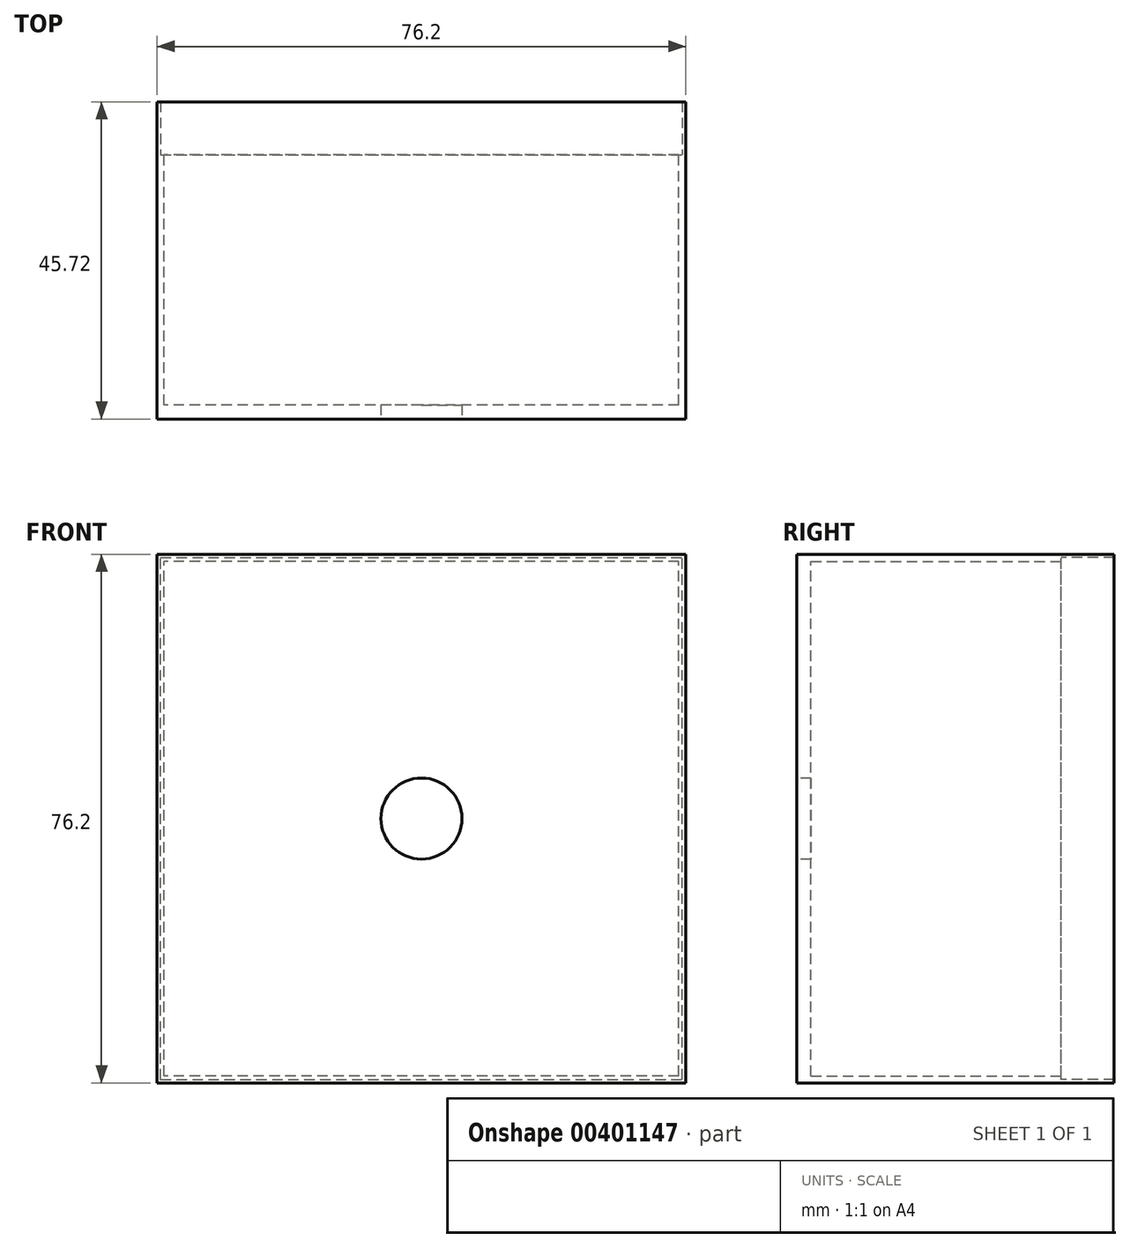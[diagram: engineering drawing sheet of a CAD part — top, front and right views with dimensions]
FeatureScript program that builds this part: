
annotation { "Feature Type Name" : "Feature", "Feature Type Description" : "" }
export const myFeature = defineFeature(function(context is Context, id is Id, definition is map)
    precondition{}
    {
        {
            var Q0;
            Q0=qCreatedBy(makeId("Front.planeOp"),FACE);
            var sketch = newSketch(context, id + "F0", { "sketchPlane" : qUnion([Q0])});
            skLineSegment(sketch, "E0.bottom", {"start": v(38.1, -38.1) * mm, "end": v(-38.1, -38.1) * mm});
            skLineSegment(sketch, "E0.top", {"start": v(38.1, 38.1) * mm, "end": v(-38.1, 38.1) * mm});
            skLineSegment(sketch, "E0.left", {"start": v(38.1, -38.1) * mm, "end": v(38.1, 38.1) * mm});
            skLineSegment(sketch, "E0.right", {"start": v(-38.1, -38.1) * mm, "end": v(-38.1, 38.1) * mm});
            skPoint(sketch, "E0.middle", {"position": v(0, 0) * mm});
            skSolve(sketch);
        }
        {
            var Q0;
            Q0=makeQuery(id+"F0.imprint","IMPRINT",FACE,{"disambiguationData":[TD([[makeQuery(id+"F0.imprint","IMPRINT",EDGE,{"derivedFrom":sQuery(id+"F0.wireOp",EDGE,"E0.bottom")}),-1.0]])]});
            extrude(context, id + "F1", {"entities" : qUnion([Q0]), "depth" : 38.1 * mm});
        }
        {
            var Q0;
            Q0=makeQuery(id+"F1.opExtrude","CAP_FACE",FACE,{"disambiguationData":[OSD([sQuery(id+"F0.wireOp",EDGE,"E0.bottom"),sQuery(id+"F0.wireOp",EDGE,"E0.top"),sQuery(id+"F0.wireOp",EDGE,"E0.left"),sQuery(id+"F0.wireOp",EDGE,"E0.right")])],"isStart":true});
            var sketch = newSketch(context, id + "F2", { "sketchPlane" : qUnion([Q0])});
            skLineSegment(sketch, "E1.bottom", {"start": v(-37.08, -37.08) * mm, "end": v(37.08, -37.08) * mm});
            skLineSegment(sketch, "E1.top", {"start": v(-37.08, 37.08) * mm, "end": v(37.08, 37.08) * mm});
            skLineSegment(sketch, "E1.left", {"start": v(-37.08, -37.08) * mm, "end": v(-37.08, 37.08) * mm});
            skLineSegment(sketch, "E1.right", {"start": v(37.08, -37.08) * mm, "end": v(37.08, 37.08) * mm});
            skPoint(sketch, "E1.middle", {"position": v(0, 0) * mm});
            skSolve(sketch);
        }
        {
            var Q0;
            Q0=makeQuery(id+"F2.imprint","IMPRINT",FACE,{"disambiguationData":[TD([[makeQuery(id+"F2.imprint","IMPRINT",EDGE,{"derivedFrom":sQuery(id+"F2.wireOp",EDGE,"E1.bottom")}),1.0]])]});
            extrude(context, id + "F3", {"entities" : qUnion([Q0]), "operationType" : NewBodyOperationType.REMOVE, "oppositeDirection" : true, "depth" : 36.07 * mm});
        }
        {
            var Q0;
            Q0=makeQuery(id+"F1.opExtrude","CAP_FACE",FACE,{"disambiguationData":[OSD([sQuery(id+"F0.wireOp",EDGE,"E0.bottom"),sQuery(id+"F0.wireOp",EDGE,"E0.top"),sQuery(id+"F0.wireOp",EDGE,"E0.left"),sQuery(id+"F0.wireOp",EDGE,"E0.right")])],"isStart":true});
            var sketch = newSketch(context, id + "F4", { "sketchPlane" : qUnion([Q0])});
            skLineSegment(sketch, "E2.bottom", {"start": v(37.6, -37.6) * mm, "end": v(-37.6, -37.6) * mm});
            skLineSegment(sketch, "E2.top", {"start": v(37.6, 37.6) * mm, "end": v(-37.6, 37.6) * mm});
            skLineSegment(sketch, "E2.left", {"start": v(37.6, -37.6) * mm, "end": v(37.6, 37.6) * mm});
            skLineSegment(sketch, "E2.right", {"start": v(-37.6, -37.6) * mm, "end": v(-37.6, 37.6) * mm});
            skPoint(sketch, "E2.middle", {"position": v(0, 0) * mm});
            skLineSegment(sketch, "E3.top", {"start": v(37.08, 37.08) * mm, "end": v(-37.08, 37.08) * mm});
            skLineSegment(sketch, "E3.right", {"start": v(-37.08, -37.08) * mm, "end": v(-37.08, 37.08) * mm});
            skLineSegment(sketch, "E4.bottom", {"start": v(38.1, -38.1) * mm, "end": v(-38.1, -38.1) * mm});
            skLineSegment(sketch, "E4.top", {"start": v(38.1, 38.1) * mm, "end": v(-38.1, 38.1) * mm});
            skLineSegment(sketch, "E4.left", {"start": v(38.1, -38.1) * mm, "end": v(38.1, 38.1) * mm});
            skLineSegment(sketch, "E4.right", {"start": v(-38.1, -38.1) * mm, "end": v(-38.1, 38.1) * mm});
            skSolve(sketch);
        }
        {
            var Q0;
            Q0 = qSketchRegion(id + "F4", true);
            extrude(context, id + "F5", {"entities" : qUnion([Q0]), "operationType" : NewBodyOperationType.ADD, "depth" : 7.62 * mm});
        }
        {
            var Q0;
            Q0=makeQuery(id+"F1.opExtrude","CAP_FACE",FACE,{"disambiguationData":[OSD([sQuery(id+"F0.wireOp",EDGE,"E0.bottom"),sQuery(id+"F0.wireOp",EDGE,"E0.top"),sQuery(id+"F0.wireOp",EDGE,"E0.left"),sQuery(id+"F0.wireOp",EDGE,"E0.right")])],"isStart":false});
            var sketch = newSketch(context, id + "F6", { "sketchPlane" : qUnion([Q0])});
            skCircle(sketch, "E5", {"center": v(0, 0) * mm, "radius": 5.84 * mm});
            skSolve(sketch);
        }
        {
            var Q0;
            Q0 = qSketchRegion(id + "F6", true);
            extrude(context, id + "F7", {"entities" : qUnion([Q0]), "operationType" : NewBodyOperationType.REMOVE, "oppositeDirection" : true, "depth" : 12.7 * mm});
        }
    });
